# Revit family: Security_MasterStation_AiPhone_GT-1A
name_source: partatom
category: Generic Models
units: mm (PartAtom-declared; Revit-internal decimal feet)

## family parameters
Can host rebar = No
Classification Number = 23.85.30.11.27
Cut with Voids When Loaded = No
Host = Face
Maintain Annotation Orientation = No
Part Type = Normal
Room Calculation Point = No
Round Connector Dimension = Use Diameter
Shared = No

## types (1)
- as Specified
    Assembly Code = D5030900
    Button Material = Plastic - Aiphone - Gray
    Construction Details = http://www.arcat.com
    Default Elevation = 0' - 0"
    Description = Aiphone Audio Tenant Station - GT-1A as Specified
    Expected Lifespan (Years) = 0
    Faceplate Material = Plastic - Aiphone - White
    Flush Mount = Yes
    Green Building-LEED = http://www.arcat.com
    Installation-Fabrication = http://www.aiphone.com
    Keynote = 13700
    Maintenance Schedule (Months) = 0
    Manufacturer = Aiphone Corp.
    Manufacturer Fax = 425-455-0071
    Manufacturer Website = http://www.aiphone.com
    Model = GT-1A
    Operating Temperature Range = 32 - 104 F
    Power Source = Powered by Control Unit
    Product Data = http://www.arcat.com
    Revision = R1_2015-05
    Sales Information = http://www.aiphone.com
    Send Message = http://www.arcat.com
    Specification = http://www.arcat.com
    Standards Conformance = as Specified
    Surface Mount = No
    Talk Button Material = Plastic - Aiphone - Red
    URL = http://www.aiphone.com
    Unit Depth = 0' - 1 1/4"
    Unit Height = 0' - 6 7/8"
    Unit Width = 0' - 4 15/16"
    Warranty Duration (Years) = 0

## geometry (parser evidence)
native form markers: Blend x6, Sweep x2
no freeform markers — native parametric forms only
